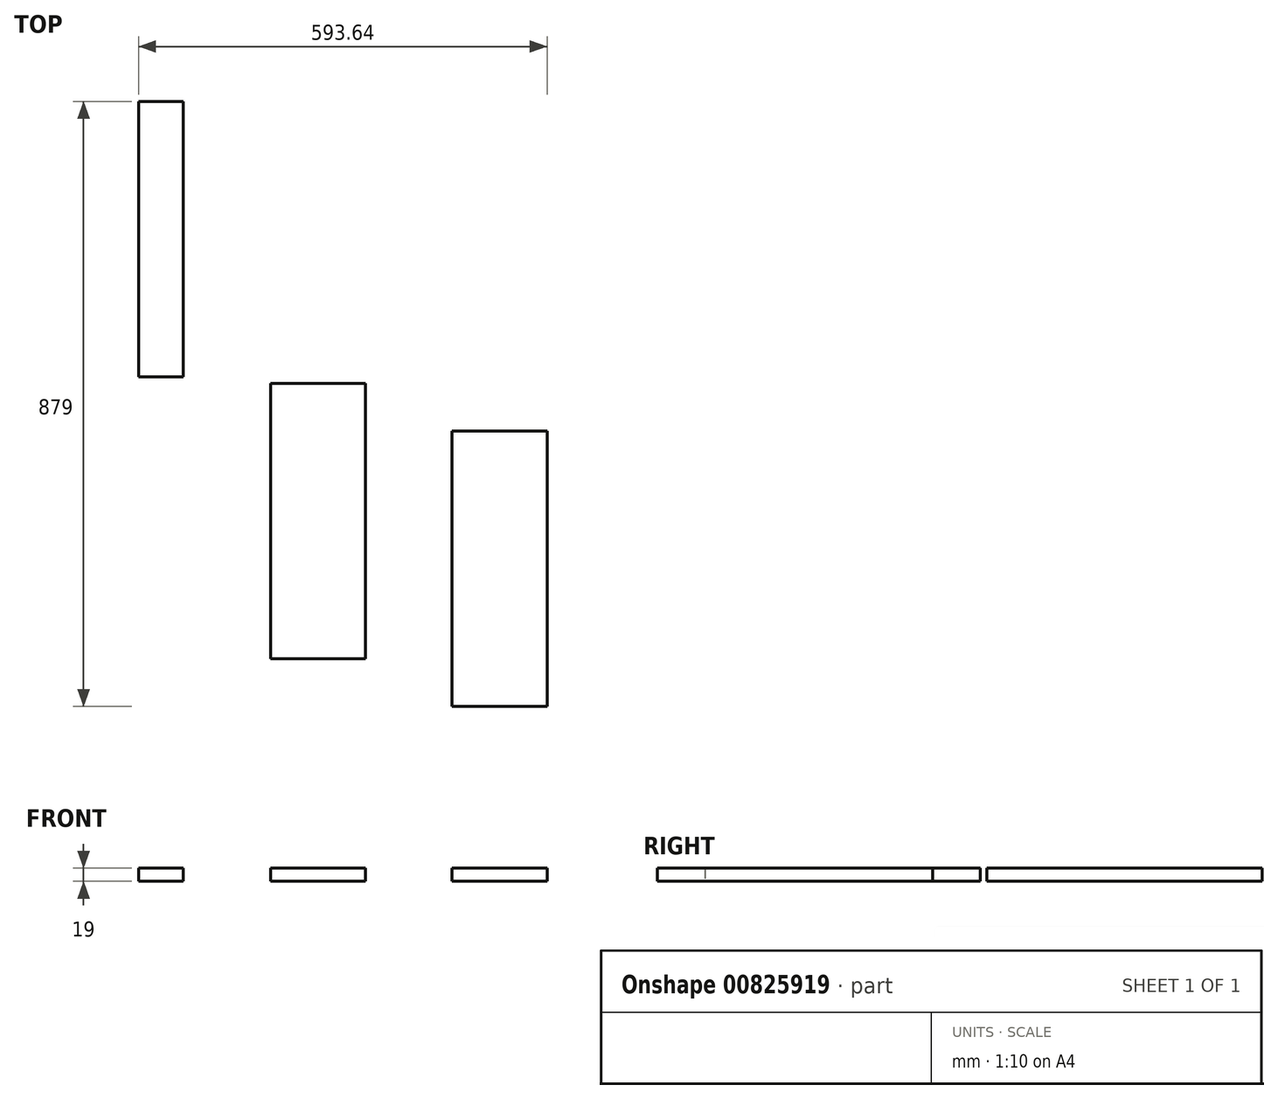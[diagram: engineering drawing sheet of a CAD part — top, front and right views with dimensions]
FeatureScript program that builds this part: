
annotation { "Feature Type Name" : "Feature", "Feature Type Description" : "" }
export const myFeature = defineFeature(function(context is Context, id is Id, definition is map)
    precondition{}
    {
        {
            var Q0;
            Q0=qCreatedBy(makeId("Top.planeOp"),FACE);
            var sketch = newSketch(context, id + "F0", { "sketchPlane" : qUnion([Q0])});
            skLineSegment(sketch, "E0.bottom", {"start": v(-125.96, -409.87) * mm, "end": v(-263.96, -409.87) * mm});
            skLineSegment(sketch, "E0.top", {"start": v(-125.96, -809.87) * mm, "end": v(-263.96, -809.87) * mm});
            skLineSegment(sketch, "E0.left", {"start": v(-125.96, -409.87) * mm, "end": v(-125.96, -809.87) * mm});
            skLineSegment(sketch, "E0.right", {"start": v(-263.96, -409.87) * mm, "end": v(-263.96, -809.87) * mm});
            skSolve(sketch);
        }
        {
            var Q0;
            Q0=qCreatedBy(makeId("Top.planeOp"),FACE);
            var sketch = newSketch(context, id + "F1", { "sketchPlane" : qUnion([Q0])});
            skLineSegment(sketch, "E1.bottom", {"start": v(0, -479.38) * mm, "end": v(138, -479.38) * mm});
            skLineSegment(sketch, "E1.top", {"start": v(0, -879.38) * mm, "end": v(138, -879.38) * mm});
            skLineSegment(sketch, "E1.left", {"start": v(0, -479.38) * mm, "end": v(0, -879.38) * mm});
            skLineSegment(sketch, "E1.right", {"start": v(138, -479.38) * mm, "end": v(138, -879.38) * mm});
            skSolve(sketch);
        }
        {
            var Q0;
            Q0=qCreatedBy(makeId("Top.planeOp"),FACE);
            var sketch = newSketch(context, id + "F2", { "sketchPlane" : qUnion([Q0])});
            skLineSegment(sketch, "E2.bottom", {"start": v(-390.64, -0.38) * mm, "end": v(-455.64, -0.38) * mm});
            skLineSegment(sketch, "E2.top", {"start": v(-390.64, -400.38) * mm, "end": v(-455.64, -400.38) * mm});
            skLineSegment(sketch, "E2.left", {"start": v(-390.64, -0.38) * mm, "end": v(-390.64, -400.38) * mm});
            skLineSegment(sketch, "E2.right", {"start": v(-455.64, -0.38) * mm, "end": v(-455.64, -400.38) * mm});
            skSolve(sketch);
        }
        {
            var Q0;
            Q0=makeQuery(id+"F2.imprint","IMPRINT",FACE,{"disambiguationData":[TD([[makeQuery(id+"F2.imprint","IMPRINT",EDGE,{"derivedFrom":sQuery(id+"F2.wireOp",EDGE,"E2.bottom")}),1.0]])]});
            var Q1;
            Q1=makeQuery(id+"F0.imprint","IMPRINT",FACE,{"disambiguationData":[TD([[makeQuery(id+"F0.imprint","IMPRINT",EDGE,{"derivedFrom":sQuery(id+"F0.wireOp",EDGE,"E0.bottom")}),1.0]])]});
            var Q2;
            Q2=makeQuery(id+"F1.imprint","IMPRINT",FACE,{"disambiguationData":[TD([[makeQuery(id+"F1.imprint","IMPRINT",EDGE,{"derivedFrom":sQuery(id+"F1.wireOp",EDGE,"E1.bottom")}),-1.0]])]});
            extrude(context, id + "F3", {"entities" : qUnion([Q0, Q1, Q2]), "depth" : 19 * mm, "offsetDistance" : 25 * mm});
        }
    });
